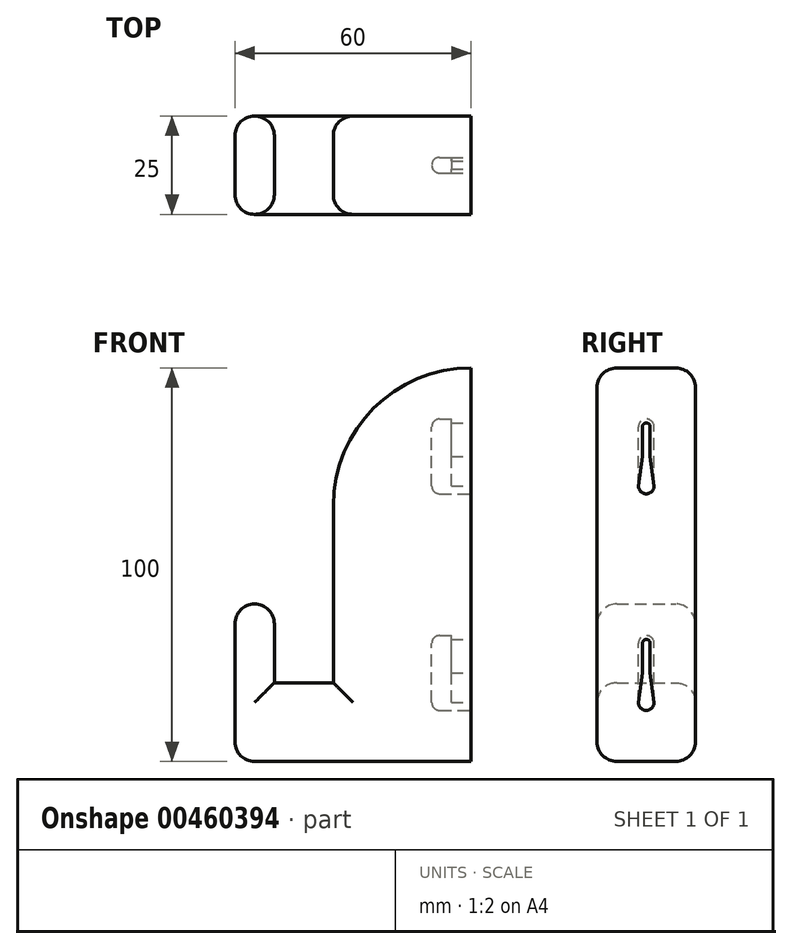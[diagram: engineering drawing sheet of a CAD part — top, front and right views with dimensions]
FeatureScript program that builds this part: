
annotation { "Feature Type Name" : "Feature", "Feature Type Description" : "" }
export const myFeature = defineFeature(function(context is Context, id is Id, definition is map)
    precondition{}
    {
        {
            var Q0;
            Q0=qCreatedBy(makeId("Front.planeOp"),FACE);
            var sketch = newSketch(context, id + "F0", { "sketchPlane" : qUnion([Q0])});
            skLineSegment(sketch, "E0", {"start": v(-30, 0) * mm, "end": v(30, 0) * mm});
            skLineSegment(sketch, "E1", {"start": v(30, 0) * mm, "end": v(30, 100) * mm});
            skLineSegment(sketch, "E2", {"start": v(30, 100) * mm, "end": v(-5, 100) * mm});
            skLineSegment(sketch, "E3", {"start": v(-5, 100) * mm, "end": v(-5, 20) * mm});
            skLineSegment(sketch, "E4", {"start": v(-5, 20) * mm, "end": v(-20, 20) * mm});
            skLineSegment(sketch, "E5", {"start": v(-20, 20) * mm, "end": v(-20, 40) * mm});
            skLineSegment(sketch, "E6", {"start": v(-20, 40) * mm, "end": v(-30, 40) * mm});
            skLineSegment(sketch, "E7", {"start": v(-30, 40) * mm, "end": v(-30, 0) * mm});
            skSolve(sketch);
        }
        {
            var Q0;
            Q0=qSketchRegion(id+"F0",true);
            extrude(context, id + "F1", {"entities" : qUnion([Q0]), "endBound" : BoundingType.SYMMETRIC, "depth" : 25 * mm});
        }
        {
            var Q0;
            Q0=makeQuery(id+"F1.opExtrude","SWEPT_EDGE",EDGE,{"disambiguationData":[OSD([sQuery(id+"F0.wireOp",EDGE,"E6"),sQuery(id+"F0.wireOp",EDGE,"E7")])]});
            var Q1;
            Q1=makeQuery(id+"F1.opExtrude","SWEPT_EDGE",EDGE,{"disambiguationData":[OSD([sQuery(id+"F0.wireOp",EDGE,"E0"),sQuery(id+"F0.wireOp",EDGE,"E7")])]});
            var Q2;
            Q2=makeQuery(id+"F1.opExtrude","SWEPT_EDGE",EDGE,{"disambiguationData":[OSD([sQuery(id+"F0.wireOp",EDGE,"E5"),sQuery(id+"F0.wireOp",EDGE,"E6")])]});
            var Q3;
            Q3=makeQuery(id+"F1.opExtrude","CAP_EDGE",EDGE,{"disambiguationData":[OSD([sQuery(id+"F0.wireOp",EDGE,"E4")])],"isStart":false});
            var Q4;
            Q4=makeQuery(id+"F1.opExtrude","CAP_EDGE",EDGE,{"disambiguationData":[OSD([sQuery(id+"F0.wireOp",EDGE,"E4")])],"isStart":true});
            var Q5;
            Q5=makeQuery(id+"F1.opExtrude","CAP_EDGE",EDGE,{"disambiguationData":[OSD([sQuery(id+"F0.wireOp",EDGE,"E7")])],"isStart":false});
            var Q6;
            Q6=makeQuery(id+"F1.opExtrude","CAP_EDGE",EDGE,{"disambiguationData":[OSD([sQuery(id+"F0.wireOp",EDGE,"E5")])],"isStart":false});
            var Q7;
            Q7=makeQuery(id+"F1.opExtrude","CAP_EDGE",EDGE,{"disambiguationData":[OSD([sQuery(id+"F0.wireOp",EDGE,"E6")])],"isStart":false});
            var Q8;
            Q8=makeQuery(id+"F1.opExtrude","CAP_EDGE",EDGE,{"disambiguationData":[OSD([sQuery(id+"F0.wireOp",EDGE,"E6")])],"isStart":true});
            var Q9;
            Q9=makeQuery(id+"F1.opExtrude","CAP_EDGE",EDGE,{"disambiguationData":[OSD([sQuery(id+"F0.wireOp",EDGE,"E7")])],"isStart":true});
            var Q10;
            Q10=makeQuery(id+"F1.opExtrude","CAP_EDGE",EDGE,{"disambiguationData":[OSD([sQuery(id+"F0.wireOp",EDGE,"E5")])],"isStart":true});
            var Q11;
            Q11=makeQuery(id+"F1.opExtrude","CAP_EDGE",EDGE,{"disambiguationData":[OSD([sQuery(id+"F0.wireOp",EDGE,"E0")])],"isStart":false});
            var Q12;
            Q12=makeQuery(id+"F1.opExtrude","CAP_EDGE",EDGE,{"disambiguationData":[OSD([sQuery(id+"F0.wireOp",EDGE,"E0")])],"isStart":true});
            var Q13;
            Q13=makeQuery(id+"F1.opExtrude","CAP_EDGE",EDGE,{"disambiguationData":[OSD([sQuery(id+"F0.wireOp",EDGE,"E3")])],"isStart":false});
            var Q14;
            Q14=makeQuery(id+"F1.opExtrude","CAP_EDGE",EDGE,{"disambiguationData":[OSD([sQuery(id+"F0.wireOp",EDGE,"E3")])],"isStart":true});
            var Q15;
            Q15=makeQuery(id+"F1.opExtrude","CAP_EDGE",EDGE,{"disambiguationData":[OSD([sQuery(id+"F0.wireOp",EDGE,"E2")])],"isStart":false});
            var Q16;
            Q16=makeQuery(id+"F1.opExtrude","CAP_EDGE",EDGE,{"disambiguationData":[OSD([sQuery(id+"F0.wireOp",EDGE,"E2")])],"isStart":true});
            fillet(context, id + "F2", {"entities" : qUnion([Q0, Q1, Q2, Q3, Q4, Q5, Q6, Q7, Q8, Q9, Q10, Q11, Q12, Q13, Q14, Q15, Q16]), "radius" : 5 * mm, "tangentPropagation" : true, "allowEdgeOverflow" : false});
        }
        {
            var Q0;
            Q0=makeQuery(id+"F1.opExtrude","SWEPT_EDGE",EDGE,{"disambiguationData":[OSD([sQuery(id+"F0.wireOp",EDGE,"E2"),sQuery(id+"F0.wireOp",EDGE,"E3")])]});
            fillet(context, id + "F3", {"entities" : qUnion([Q0]), "radius" : 35 * mm, "tangentPropagation" : true, "allowEdgeOverflow" : false});
        }
        {
            var Q0;
            Q0=makeQuery(id+"F1.opExtrude","SWEPT_FACE",FACE,{"disambiguationData":[OSD([sQuery(id+"F0.wireOp",EDGE,"E1")])]});
            var sketch = newSketch(context, id + "F4", { "sketchPlane" : qUnion([Q0])});
            skLineSegment(sketch, "E8", {"start": v(0, 15) * mm, "end": v(0, 30) * mm});
            skPoint(sketch, "E8.startSnap0", {"position": v(0, 0) * mm});
            skLineSegment(sketch, "E9", {"start": v(0, 70) * mm, "end": v(0, 85) * mm});
            skArc(sketch, "E10.0.startCap", {"start": v(2, 15) * mm, "mid": v(0, 13) * mm, "end": v(-2, 15) * mm});
            skArc(sketch, "E10.0.endCap", {"start": v(-2, 30) * mm, "mid": v(0, 32) * mm, "end": v(2, 30) * mm});
            skLineSegment(sketch, "E10.0.left", {"start": v(-2, 15) * mm, "end": v(-2, 30) * mm});
            skLineSegment(sketch, "E10.0.right", {"start": v(2, 15) * mm, "end": v(2, 30) * mm});
            skArc(sketch, "E10.1.startCap", {"start": v(2, 70) * mm, "mid": v(0, 68) * mm, "end": v(-2, 70) * mm});
            skArc(sketch, "E10.1.endCap", {"start": v(-2, 85) * mm, "mid": v(0, 87) * mm, "end": v(2, 85) * mm});
            skLineSegment(sketch, "E10.1.left", {"start": v(-2, 70) * mm, "end": v(-2, 85) * mm});
            skLineSegment(sketch, "E10.1.right", {"start": v(2, 70) * mm, "end": v(2, 85) * mm});
            skSolve(sketch);
        }
        {
            var Q0;
            Q0=qSketchRegion(id+"F4",true);
            extrude(context, id + "F5", {"entities" : qUnion([Q0]), "operationType" : NewBodyOperationType.REMOVE, "oppositeDirection" : true, "depth" : 10 * mm});
        }
        {
            var Q0;
            Q0=makeQuery(id+"F1.opExtrude","SWEPT_FACE",FACE,{"disambiguationData":[OSD([sQuery(id+"F0.wireOp",EDGE,"E1")])]});
            var sketch = newSketch(context, id + "F6", { "sketchPlane" : qUnion([Q0])});
            skArc(sketch, "E11", {"start": v(1, 30) * mm, "mid": v(0, 31) * mm, "end": v(-1, 30) * mm});
            skLineSegment(sketch, "E12", {"start": v(2, 15) * mm, "end": v(2, 30) * mm});
            skArc(sketch, "E13", {"start": v(2, 30) * mm, "mid": v(0, 32) * mm, "end": v(-2, 30) * mm});
            skLineSegment(sketch, "E14", {"start": v(-2, 30) * mm, "end": v(-2, 15) * mm});
            skLineSegment(sketch, "E15", {"start": v(-2, 15) * mm, "end": v(-1, 22.5) * mm});
            skLineSegment(sketch, "E16", {"start": v(-1, 22.5) * mm, "end": v(-1, 30) * mm});
            skLineSegment(sketch, "E17", {"start": v(1, 30) * mm, "end": v(1, 22.5) * mm});
            skLineSegment(sketch, "E18", {"start": v(1, 22.5) * mm, "end": v(2, 15) * mm});
            skLineSegment(sketch, "E19.0.1.0", {"start": v(1, 77.5) * mm, "end": v(2, 70) * mm});
            skLineSegment(sketch, "E19.0.1.1", {"start": v(-1, 77.5) * mm, "end": v(-1, 85) * mm});
            skLineSegment(sketch, "E19.0.1.2", {"start": v(-2, 70) * mm, "end": v(-1, 77.5) * mm});
            skLineSegment(sketch, "E19.0.1.3", {"start": v(1, 85) * mm, "end": v(1, 77.5) * mm});
            skArc(sketch, "E19.0.1.4", {"start": v(1, 85) * mm, "mid": v(0, 86) * mm, "end": v(-1, 85) * mm});
            skLineSegment(sketch, "E19.0.1.5", {"start": v(2, 70) * mm, "end": v(2, 85) * mm});
            skLineSegment(sketch, "E19.0.1.6", {"start": v(-2, 85) * mm, "end": v(-2, 70) * mm});
            skArc(sketch, "E19.0.1.7", {"start": v(2, 85) * mm, "mid": v(0, 87) * mm, "end": v(-2, 85) * mm});
            skLineSegment(sketch, "E19.direction1", {"start": v(-2, 15) * mm, "end": v(23, 15) * mm, "construction": true});
            skLineSegment(sketch, "E19.direction2", {"start": v(-2, 15) * mm, "end": v(-2, 70) * mm, "construction": true});
            skSolve(sketch);
        }
        {
            var Q0;
            Q0=qSketchRegion(id+"F6",true);
            extrude(context, id + "F7", {"entities" : qUnion([Q0]), "operationType" : NewBodyOperationType.ADD, "oppositeDirection" : true, "depth" : 5 * mm});
        }
        {
            var Q0;
            Q0=makeQuery(id+"F5.boolean.opBoolean","COPY",FACE,{"derivedFrom":makeQuery(id+"F5.opExtrude","CAP_FACE",FACE,{"disambiguationData":[OSD([sQuery(id+"F4.wireOp",EDGE,"E10.0.startCap"),sQuery(id+"F4.wireOp",EDGE,"E10.0.endCap"),sQuery(id+"F4.wireOp",EDGE,"E10.0.left"),sQuery(id+"F4.wireOp",EDGE,"E10.0.right")])],"isStart":false})});
            var Q1;
            Q1=makeQuery(id+"F5.boolean.opBoolean","COPY",FACE,{"derivedFrom":makeQuery(id+"F5.opExtrude","CAP_FACE",FACE,{"disambiguationData":[OSD([sQuery(id+"F4.wireOp",EDGE,"E10.1.startCap"),sQuery(id+"F4.wireOp",EDGE,"E10.1.endCap"),sQuery(id+"F4.wireOp",EDGE,"E10.1.left"),sQuery(id+"F4.wireOp",EDGE,"E10.1.right")])],"isStart":false})});
            fillet(context, id + "F8", {"entities" : qUnion([Q0, Q1]), "radius" : 2 * mm, "tangentPropagation" : true, "allowEdgeOverflow" : false});
        }
    });
